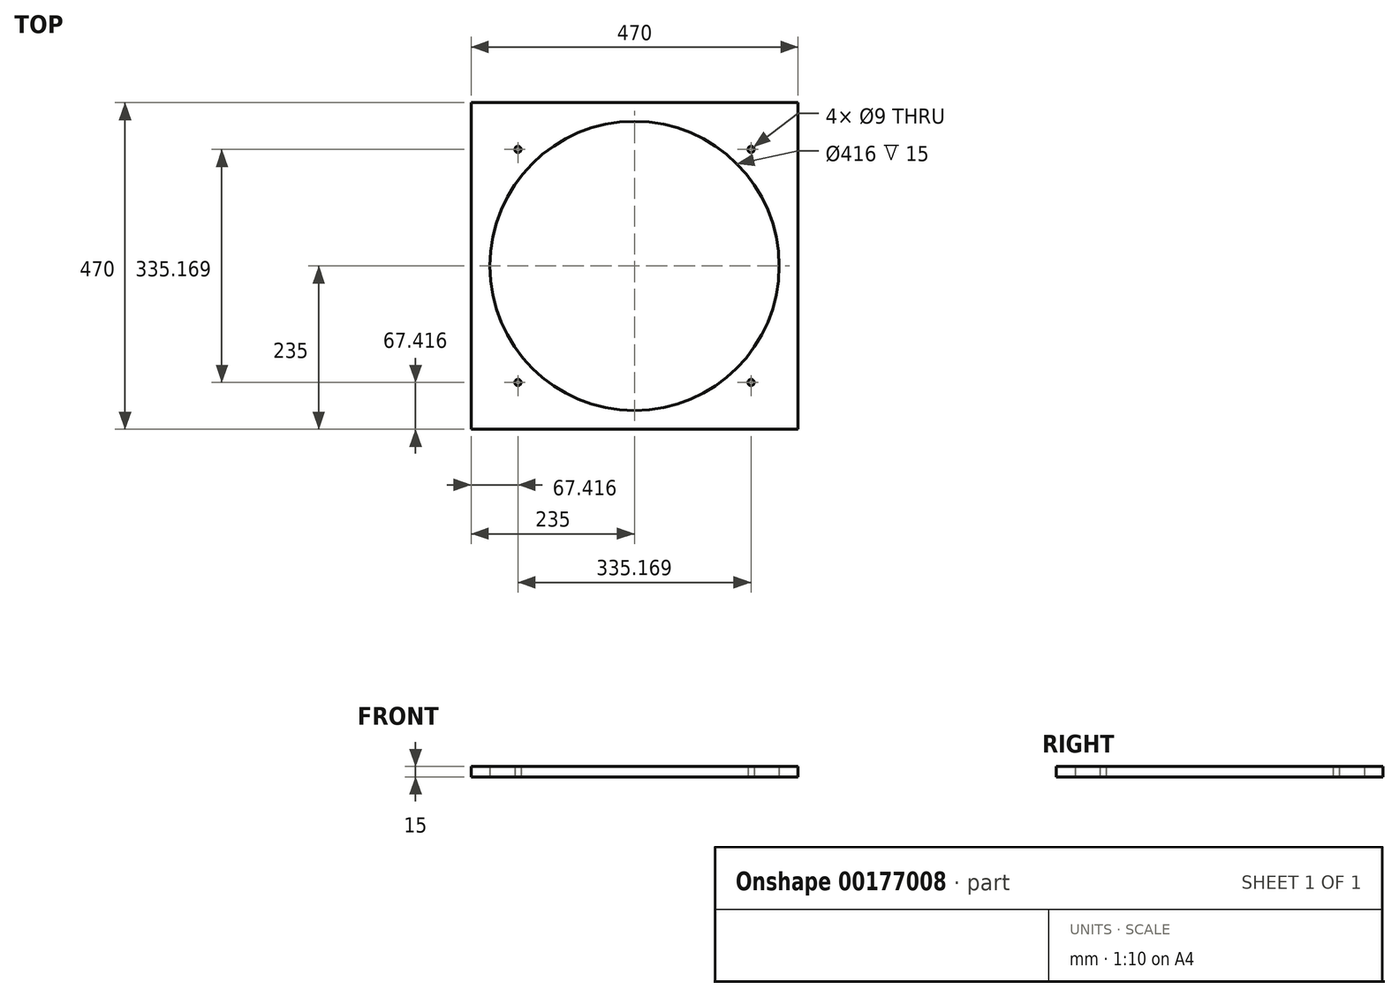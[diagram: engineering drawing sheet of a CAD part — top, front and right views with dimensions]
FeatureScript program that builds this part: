
annotation { "Feature Type Name" : "Feature", "Feature Type Description" : "" }
export const myFeature = defineFeature(function(context is Context, id is Id, definition is map)
    precondition{}
    {
        {
            var Q0;
            Q0=qCreatedBy(makeId("Top.planeOp"),FACE);
            var sketch = newSketch(context, id + "F0", { "sketchPlane" : qUnion([Q0])});
            skLineSegment(sketch, "E0.bottom", {"start": v(235, 235) * mm, "end": v(-235, 235) * mm});
            skLineSegment(sketch, "E0.top", {"start": v(235, -235) * mm, "end": v(-235, -235) * mm});
            skLineSegment(sketch, "E0.left", {"start": v(235, 235) * mm, "end": v(235, -235) * mm});
            skLineSegment(sketch, "E0.right", {"start": v(-235, 235) * mm, "end": v(-235, -235) * mm});
            skPoint(sketch, "E0.middle", {"position": v(0, 0) * mm});
            skLineSegment(sketch, "E1", {"start": v(-235, 235) * mm, "end": v(235, -235) * mm, "construction": true});
            skLineSegment(sketch, "E2", {"start": v(-235, -235) * mm, "end": v(235, 235) * mm, "construction": true});
            skCircle(sketch, "E3", {"center": v(0, 0) * mm, "radius": 208 * mm});
            skCircle(sketch, "E4", {"center": v(0, 0) * mm, "radius": 237 * mm, "construction": true});
            skCircle(sketch, "E5", {"center": v(-167.58, 167.58) * mm, "radius": 4.5 * mm});
            skCircle(sketch, "E6", {"center": v(167.58, 167.58) * mm, "radius": 4.5 * mm});
            skCircle(sketch, "E7", {"center": v(167.58, -167.58) * mm, "radius": 4.5 * mm});
            skCircle(sketch, "E8", {"center": v(-167.58, -167.58) * mm, "radius": 4.5 * mm});
            skSolve(sketch);
        }
        {
            var Q0;
            Q0=makeQuery(id+"F0.imprint","IMPRINT",FACE,{"disambiguationData":[TD([[makeQuery(id+"F0.imprint","IMPRINT",EDGE,{"derivedFrom":sQuery(id+"F0.wireOp",EDGE,"E0.bottom")}),1.0]])]});
            extrude(context, id + "F1", {"entities" : qUnion([Q0]), "depth" : 15 * mm});
        }
    });
